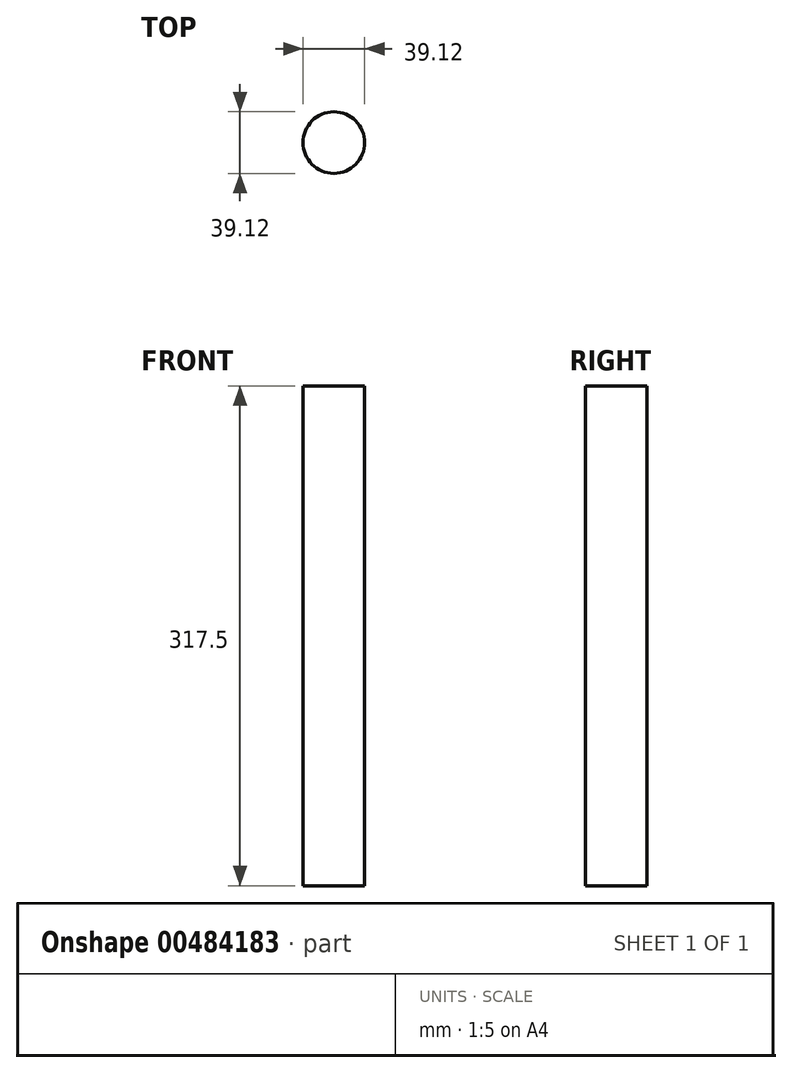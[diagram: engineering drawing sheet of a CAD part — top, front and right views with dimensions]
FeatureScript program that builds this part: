
annotation { "Feature Type Name" : "Feature", "Feature Type Description" : "" }
export const myFeature = defineFeature(function(context is Context, id is Id, definition is map)
    precondition{}
    {
        {
            var Q0;
            Q0=qCreatedBy(makeId("Top.planeOp"),FACE);
            var sketch = newSketch(context, id + "F0", { "sketchPlane" : qUnion([Q0])});
            skCircle(sketch, "E0", {"center": v(-262.76, -34.55) * mm, "radius": 19.56 * mm});
            skSolve(sketch);
        }
        {
            var Q0;
            Q0=sQuery(id+"F0.wireOp",EDGE,"E0");
            extrude(context, id + "F1", {"bodyType" : ToolBodyType.SURFACE, "surfaceEntities" : qUnion([Q0]), "depth" : 317.5 * mm});
        }
    });
